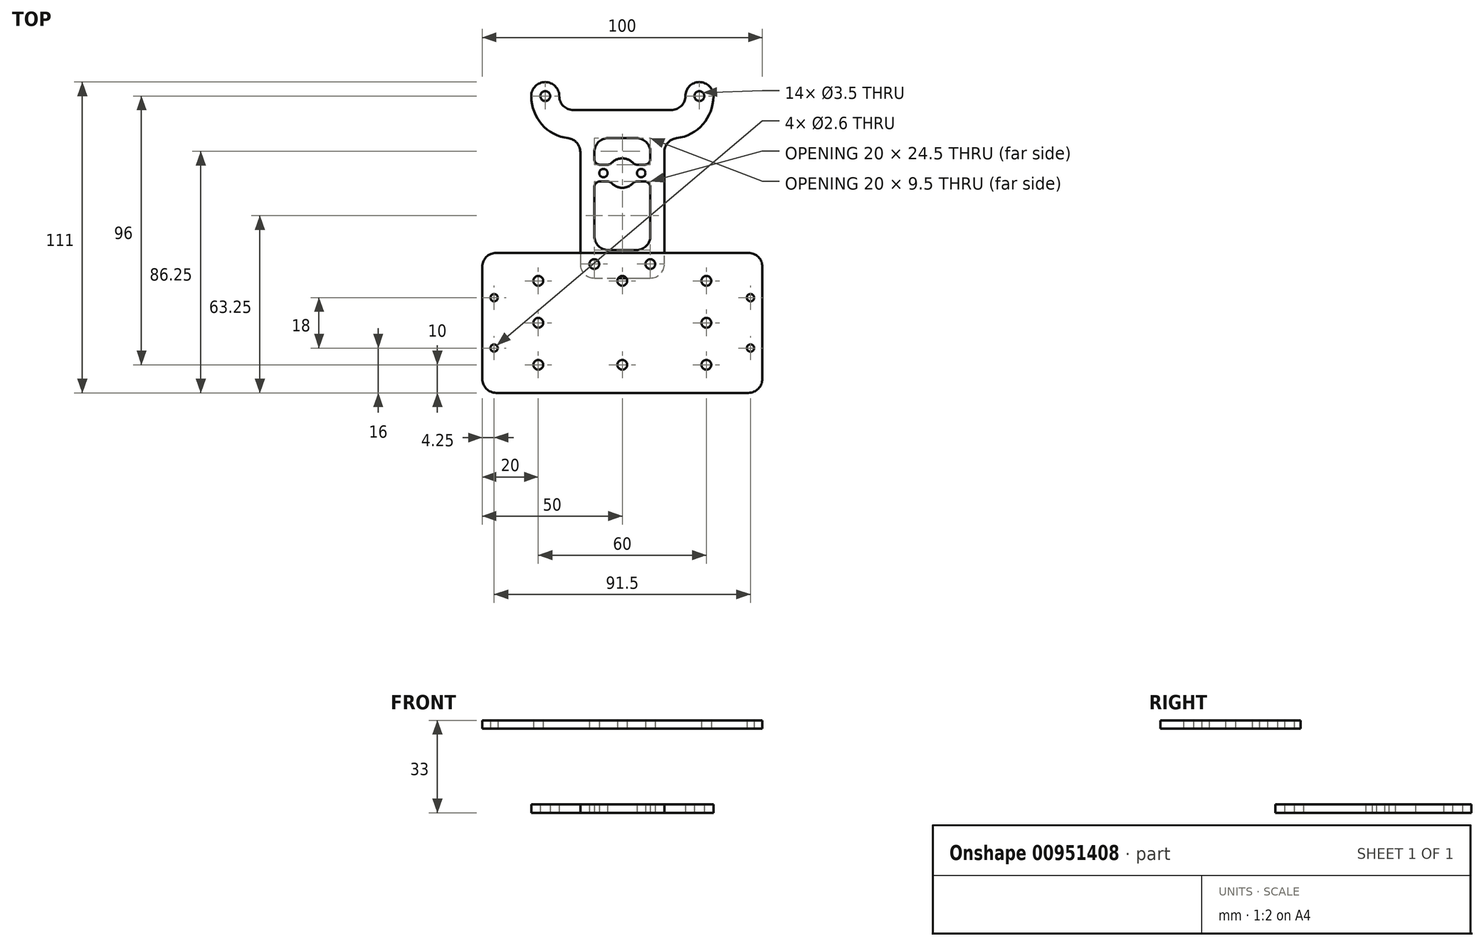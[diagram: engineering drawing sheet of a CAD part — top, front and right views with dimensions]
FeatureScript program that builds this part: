
annotation { "Feature Type Name" : "Feature", "Feature Type Description" : "" }
export const myFeature = defineFeature(function(context is Context, id is Id, definition is map)
    precondition{}
    {
        {
            var Q0;
            Q0=qCreatedBy(makeId("Top.planeOp"),FACE);
            cPlane(context, id + "F0", {"entities" : qUnion([Q0]), "cplaneType" : CPlaneType.OFFSET, "offset" : 30 * mm, "width" : 150 * mm, "height" : 150 * mm});
        }
        {
            var Q0;
            Q0=qCreatedBy(id+"F0.planeOp",FACE);
            var sketch = newSketch(context, id + "F1", { "sketchPlane" : qUnion([Q0])});
            skLineSegment(sketch, "E0.bottom", {"start": v(-25, 30) * mm, "end": v(25, 30) * mm, "construction": true});
            skLineSegment(sketch, "E0.top", {"start": v(-25, -30) * mm, "end": v(25, -30) * mm, "construction": true});
            skLineSegment(sketch, "E0.left", {"start": v(-25, 30) * mm, "end": v(-25, -30) * mm, "construction": true});
            skLineSegment(sketch, "E0.right", {"start": v(25, 30) * mm, "end": v(25, -30) * mm, "construction": true});
            skPoint(sketch, "E0.middle", {"position": v(0, 0) * mm});
            skLineSegment(sketch, "E1.bottom", {"start": v(-60, 42.5) * mm, "end": v(-26, 42.5) * mm, "construction": true});
            skLineSegment(sketch, "E1.top", {"start": v(-60, -42.5) * mm, "end": v(-26, -42.5) * mm, "construction": true});
            skLineSegment(sketch, "E1.left", {"start": v(-60, 42.5) * mm, "end": v(-60, -42.5) * mm, "construction": true});
            skLineSegment(sketch, "E1.right", {"start": v(-26, 42.5) * mm, "end": v(-26, -42.5) * mm, "construction": true});
            skLineSegment(sketch, "E2.bottom", {"start": v(26, 42.5) * mm, "end": v(60, 42.5) * mm, "construction": true});
            skLineSegment(sketch, "E2.top", {"start": v(26, -42.5) * mm, "end": v(60, -42.5) * mm, "construction": true});
            skLineSegment(sketch, "E2.left", {"start": v(26, 42.5) * mm, "end": v(26, -42.5) * mm, "construction": true});
            skLineSegment(sketch, "E2.right", {"start": v(60, 42.5) * mm, "end": v(60, -42.5) * mm, "construction": true});
            skLineSegment(sketch, "E3", {"start": v(0, 0) * mm, "end": v(-26, 0) * mm, "construction": true});
            skLineSegment(sketch, "E4", {"start": v(0, 0) * mm, "end": v(26, 0) * mm, "construction": true});
            skLineSegment(sketch, "E5.bottom", {"start": v(-50, 25) * mm, "end": v(50, 25) * mm});
            skLineSegment(sketch, "E5.top", {"start": v(-50, -25) * mm, "end": v(50, -25) * mm});
            skLineSegment(sketch, "E5.left", {"start": v(-50, 25) * mm, "end": v(-50, 0) * mm});
            skLineSegment(sketch, "E5.right", {"start": v(50, 25) * mm, "end": v(50, 0) * mm});
            skLineSegment(sketch, "E6", {"start": v(-50, 0) * mm, "end": v(-50, -25) * mm});
            skLineSegment(sketch, "E7", {"start": v(50, 0) * mm, "end": v(50, -25) * mm});
            skCircle(sketch, "E8", {"center": v(-45.75, 9) * mm, "radius": 1.3 * mm});
            skCircle(sketch, "E9", {"center": v(-45.75, -9) * mm, "radius": 1.3 * mm});
            skCircle(sketch, "E10", {"center": v(45.75, -9) * mm, "radius": 1.3 * mm});
            skCircle(sketch, "E11", {"center": v(45.75, 9) * mm, "radius": 1.3 * mm});
            skCircle(sketch, "E12", {"center": v(-30, 0) * mm, "radius": 1.75 * mm});
            skCircle(sketch, "E13", {"center": v(30, 0) * mm, "radius": 1.75 * mm});
            skCircle(sketch, "E14", {"center": v(-30, 15) * mm, "radius": 1.75 * mm});
            skCircle(sketch, "E15", {"center": v(30, 15) * mm, "radius": 1.75 * mm});
            skCircle(sketch, "E16", {"center": v(30, -15) * mm, "radius": 1.75 * mm});
            skCircle(sketch, "E17", {"center": v(-30, -15) * mm, "radius": 1.75 * mm});
            skCircle(sketch, "E18", {"center": v(0, 15) * mm, "radius": 1.75 * mm});
            skCircle(sketch, "E19", {"center": v(0, -15) * mm, "radius": 1.75 * mm});
            skCircle(sketch, "E20", {"center": v(-10, 21) * mm, "radius": 1.75 * mm});
            skCircle(sketch, "E21", {"center": v(10, 21) * mm, "radius": 1.75 * mm});
            skSolve(sketch);
        }
        {
            var Q0;
            Q0=makeQuery(id+"F1.imprint","IMPRINT",FACE,{"disambiguationData":[TD([[makeQuery(id+"F1.imprint","IMPRINT",EDGE,{"derivedFrom":sQuery(id+"F1.wireOp",EDGE,"E5.bottom")}),-1.0]])]});
            extrude(context, id + "F2", {"entities" : qUnion([Q0]), "depth" : 3 * mm, "offsetDistance" : 25 * mm});
        }
        {
            var Q0;
            Q0=qCreatedBy(makeId("Top.planeOp"),FACE);
            var sketch = newSketch(context, id + "F3", { "sketchPlane" : qUnion([Q0])});
            skCircle(sketch, "E22.0", {"center": v(-10, 21) * mm, "radius": 1.75 * mm});
            skCircle(sketch, "E22.1", {"center": v(10, 21) * mm, "radius": 1.75 * mm});
            skLineSegment(sketch, "E23", {"start": v(-15, 16) * mm, "end": v(15, 16) * mm});
            skLineSegment(sketch, "E24", {"start": v(15, 16) * mm, "end": v(15, 66) * mm});
            skLineSegment(sketch, "E25", {"start": v(15, 66) * mm, "end": v(32.5, 66) * mm});
            skLineSegment(sketch, "E26", {"start": v(32.5, 66) * mm, "end": v(32.5, 86) * mm});
            skLineSegment(sketch, "E27", {"start": v(32.5, 86) * mm, "end": v(22.5, 86) * mm});
            skLineSegment(sketch, "E28", {"start": v(22.5, 86) * mm, "end": v(22.5, 76) * mm});
            skLineSegment(sketch, "E29", {"start": v(22.5, 76) * mm, "end": v(-22.5, 76) * mm});
            skLineSegment(sketch, "E30", {"start": v(-22.5, 76) * mm, "end": v(-22.5, 86) * mm});
            skLineSegment(sketch, "E31", {"start": v(-22.5, 86) * mm, "end": v(-32.5, 86) * mm});
            skLineSegment(sketch, "E32", {"start": v(-32.5, 86) * mm, "end": v(-32.5, 66) * mm});
            skLineSegment(sketch, "E33", {"start": v(-32.5, 66) * mm, "end": v(-15, 66) * mm});
            skLineSegment(sketch, "E34", {"start": v(-15, 66) * mm, "end": v(-15, 16) * mm});
            skCircle(sketch, "E35", {"center": v(-27.5, 81) * mm, "radius": 1.75 * mm});
            skPoint(sketch, "E35.centerSnap0", {"position": v(-27.5, 86) * mm});
            skPoint(sketch, "E35.centerSnap1", {"position": v(-22.5, 81) * mm});
            skCircle(sketch, "E36", {"center": v(27.5, 81) * mm, "radius": 1.75 * mm});
            skPoint(sketch, "E36.centerSnap0", {"position": v(27.5, 86) * mm});
            skPoint(sketch, "E36.centerSnap1", {"position": v(22.5, 81) * mm});
            skLineSegment(sketch, "E37.bottom", {"start": v(-10, 66) * mm, "end": v(10, 66) * mm});
            skLineSegment(sketch, "E37.top", {"start": v(-10, 26) * mm, "end": v(10, 26) * mm});
            skLineSegment(sketch, "E37.left", {"start": v(-10, 66) * mm, "end": v(-10, 26) * mm});
            skLineSegment(sketch, "E37.right", {"start": v(10, 66) * mm, "end": v(10, 26) * mm});
            skCircle(sketch, "E38", {"center": v(-6.75, 53.5) * mm, "radius": 1.5 * mm});
            skCircle(sketch, "E39", {"center": v(6.75, 53.5) * mm, "radius": 1.5 * mm});
            skLineSegment(sketch, "E40", {"start": v(-6.75, 53.5) * mm, "end": v(-10, 53.5) * mm, "construction": true});
            skLineSegment(sketch, "E41", {"start": v(6.75, 53.5) * mm, "end": v(10, 53.5) * mm, "construction": true});
            skLineSegment(sketch, "E42", {"start": v(-10, 56.5) * mm, "end": v(-4.3, 56.5) * mm});
            skLineSegment(sketch, "E43", {"start": v(10, 50.5) * mm, "end": v(4.3, 50.5) * mm});
            skArc(sketch, "E44", {"start": v(-4.3, 50.5) * mm, "mid": v(0, 48.25) * mm, "end": v(4.3, 50.5) * mm});
            skPoint(sketch, "E44.centerSnap0", {"position": v(0, 66) * mm});
            skArc(sketch, "E45.trimOffspring", {"start": v(4.3, 56.5) * mm, "mid": v(0, 58.75) * mm, "end": v(-4.3, 56.5) * mm});
            skLineSegment(sketch, "E46.trimOffspring", {"start": v(4.3, 56.5) * mm, "end": v(10, 56.5) * mm});
            skLineSegment(sketch, "E47.trimOffspring", {"start": v(-4.3, 50.5) * mm, "end": v(-10, 50.5) * mm});
            skSolve(sketch);
        }
        {
            var Q0;
            Q0=makeQuery(id+"F3.imprint","IMPRINT",FACE,{"disambiguationData":[TD([[makeQuery(id+"F3.imprint","IMPRINT",EDGE,{"derivedFrom":sQuery(id+"F3.wireOp",EDGE,"E22.0")}),-1.0]])]});
            var Q1;
            {var subQ0=sQuery(id+"F3.wireOp",EDGE,"1neENVXK-yCNZ-4XRZ-Vguu-GqOuGw2G458n");Q1=makeQuery(id+"F3.imprint","IMPRINT",FACE,{"disambiguationData":[TD([[makeQuery(id+"F3.imprint","IMPRINT",EDGE,{"derivedFrom":subQ0}),-1.0]])]});}
            var Q2;
            {var subQ5=sQuery(id+"F3.wireOp",EDGE,"E38");Q2=makeQuery(id+"F3.imprint","IMPRINT",FACE,{"disambiguationData":[TD([[makeQuery(id+"F3.imprint","IMPRINT",EDGE,{"derivedFrom":subQ5}),-1.0]])]});}
            var Q3;
            {var subQ0=sQuery(id+"F3.wireOp",EDGE,"6WteCXc5-cXgC-OXwJ-sMJl-BuiwVkrk2LJA");Q3=makeQuery(id+"F3.imprint","IMPRINT",FACE,{"disambiguationData":[TD([[makeQuery(id+"F3.imprint","IMPRINT",EDGE,{"derivedFrom":subQ0}),1.0]])]});}
            extrude(context, id + "F4", {"entities" : qUnion([Q0, Q1, Q2, Q3]), "depth" : 3 * mm, "offsetDistance" : 25 * mm});
        }
        {
            var Q0;
            Q0=makeQuery(id+"F4.opExtrude","SWEPT_EDGE",EDGE,{"disambiguationData":[OSD([sQuery(id+"F3.wireOp",EDGE,"E33"),sQuery(id+"F3.wireOp",EDGE,"E34")])]});
            var Q1;
            Q1=makeQuery(id+"F4.opExtrude","SWEPT_EDGE",EDGE,{"disambiguationData":[OSD([sQuery(id+"F3.wireOp",EDGE,"E29"),sQuery(id+"F3.wireOp",EDGE,"E30")])]});
            var Q2;
            Q2=makeQuery(id+"F4.opExtrude","SWEPT_EDGE",EDGE,{"disambiguationData":[OSD([sQuery(id+"F3.wireOp",EDGE,"E30"),sQuery(id+"F3.wireOp",EDGE,"E31")])]});
            var Q3;
            Q3=makeQuery(id+"F4.opExtrude","SWEPT_EDGE",EDGE,{"disambiguationData":[OSD([sQuery(id+"F3.wireOp",EDGE,"E31"),sQuery(id+"F3.wireOp",EDGE,"E32")])]});
            var Q4;
            Q4=makeQuery(id+"F4.opExtrude","SWEPT_EDGE",EDGE,{"disambiguationData":[OSD([sQuery(id+"F3.wireOp",EDGE,"E28"),sQuery(id+"F3.wireOp",EDGE,"E29")])]});
            var Q5;
            Q5=makeQuery(id+"F4.opExtrude","SWEPT_EDGE",EDGE,{"disambiguationData":[OSD([sQuery(id+"F3.wireOp",EDGE,"E27"),sQuery(id+"F3.wireOp",EDGE,"E28")])]});
            var Q6;
            Q6=makeQuery(id+"F4.opExtrude","SWEPT_EDGE",EDGE,{"disambiguationData":[OSD([sQuery(id+"F3.wireOp",EDGE,"E26"),sQuery(id+"F3.wireOp",EDGE,"E27")])]});
            var Q7;
            Q7=makeQuery(id+"F4.opExtrude","SWEPT_EDGE",EDGE,{"disambiguationData":[OSD([sQuery(id+"F3.wireOp",EDGE,"E24"),sQuery(id+"F3.wireOp",EDGE,"E25")])]});
            var Q8;
            Q8=makeQuery(id+"F4.opExtrude","SWEPT_EDGE",EDGE,{"disambiguationData":[OSD([sQuery(id+"F3.wireOp",EDGE,"E23"),sQuery(id+"F3.wireOp",EDGE,"E24")])]});
            var Q9;
            Q9=makeQuery(id+"F4.opExtrude","SWEPT_EDGE",EDGE,{"disambiguationData":[OSD([sQuery(id+"F3.wireOp",EDGE,"E23"),sQuery(id+"F3.wireOp",EDGE,"E34")])]});
            var Q10;
            Q10=makeQuery(id+"F4.opExtrude","SWEPT_EDGE",EDGE,{"disambiguationData":[OSD([sQuery(id+"F3.wireOp",EDGE,"E37.bottom"),sQuery(id+"F3.wireOp",EDGE,"E37.left")])]});
            var Q11;
            Q11=makeQuery(id+"F4.opExtrude","SWEPT_EDGE",EDGE,{"disambiguationData":[OSD([sQuery(id+"F3.wireOp",EDGE,"E37.bottom"),sQuery(id+"F3.wireOp",EDGE,"E37.right")])]});
            var Q12;
            Q12=makeQuery(id+"F4.opExtrude","SWEPT_EDGE",EDGE,{"disambiguationData":[OSD([sQuery(id+"F3.wireOp",EDGE,"E37.top"),sQuery(id+"F3.wireOp",EDGE,"E37.right")])]});
            var Q13;
            Q13=makeQuery(id+"F4.opExtrude","SWEPT_EDGE",EDGE,{"disambiguationData":[OSD([sQuery(id+"F3.wireOp",EDGE,"E37.top"),sQuery(id+"F3.wireOp",EDGE,"E37.left")])]});
            fillet(context, id + "F5", {"entities" : qUnion([Q0, Q1, Q2, Q3, Q4, Q5, Q6, Q7, Q8, Q9, Q10, Q11, Q12, Q13]), "radius" : 5 * mm, "tangentPropagation" : true, "allowEdgeOverflow" : false});
        }
        {
            var Q0;
            Q0=makeQuery(id+"F4.opExtrude","SWEPT_EDGE",EDGE,{"disambiguationData":[OSD([sQuery(id+"F3.wireOp",EDGE,"E25"),sQuery(id+"F3.wireOp",EDGE,"E26")])]});
            var Q1;
            Q1=makeQuery(id+"F4.opExtrude","SWEPT_EDGE",EDGE,{"disambiguationData":[OSD([sQuery(id+"F3.wireOp",EDGE,"E32"),sQuery(id+"F3.wireOp",EDGE,"E33")])]});
            fillet(context, id + "F6", {"entities" : qUnion([Q0, Q1]), "radius" : 15 * mm, "tangentPropagation" : true, "allowEdgeOverflow" : false});
        }
        {
            var Q0;
            Q0=makeQuery(id+"F2.opExtrude","SWEPT_EDGE",EDGE,{"disambiguationData":[OSD([sQuery(id+"F1.wireOp",EDGE,"E5.bottom"),sQuery(id+"F1.wireOp",EDGE,"E5.left")])]});
            var Q1;
            Q1=makeQuery(id+"F2.opExtrude","SWEPT_EDGE",EDGE,{"disambiguationData":[OSD([sQuery(id+"F1.wireOp",EDGE,"E5.top"),sQuery(id+"F1.wireOp",EDGE,"E6")])]});
            var Q2;
            Q2=makeQuery(id+"F2.opExtrude","SWEPT_EDGE",EDGE,{"disambiguationData":[OSD([sQuery(id+"F1.wireOp",EDGE,"E5.top"),sQuery(id+"F1.wireOp",EDGE,"E7")])]});
            var Q3;
            Q3=makeQuery(id+"F2.opExtrude","SWEPT_EDGE",EDGE,{"disambiguationData":[OSD([sQuery(id+"F1.wireOp",EDGE,"E5.bottom"),sQuery(id+"F1.wireOp",EDGE,"E5.right")])]});
            fillet(context, id + "F7", {"entities" : qUnion([Q0, Q1, Q2, Q3]), "radius" : 5 * mm, "tangentPropagation" : true, "allowEdgeOverflow" : false});
        }
        {
            var Q0;
            Q0=makeQuery(id+"F4.opExtrude","SWEPT_EDGE",EDGE,{"disambiguationData":[OSD([sQuery(id+"F3.wireOp",EDGE,"E37.left"),sQuery(id+"F3.wireOp",EDGE,"E42")])]});
            var Q1;
            Q1=makeQuery(id+"F4.opExtrude","SWEPT_EDGE",EDGE,{"disambiguationData":[OSD([sQuery(id+"F3.wireOp",EDGE,"E37.left"),sQuery(id+"F3.wireOp",EDGE,"E47.trimOffspring")])]});
            var Q2;
            Q2=makeQuery(id+"F4.opExtrude","SWEPT_EDGE",EDGE,{"disambiguationData":[OSD([sQuery(id+"F3.wireOp",EDGE,"E37.right"),sQuery(id+"F3.wireOp",EDGE,"E43")])]});
            var Q3;
            Q3=makeQuery(id+"F4.opExtrude","SWEPT_EDGE",EDGE,{"disambiguationData":[OSD([sQuery(id+"F3.wireOp",EDGE,"E37.right"),sQuery(id+"F3.wireOp",EDGE,"E46.trimOffspring")])]});
            var Q4;
            Q4=makeQuery(id+"F4.opExtrude","SWEPT_EDGE",EDGE,{"disambiguationData":[OSD([sQuery(id+"F3.wireOp",EDGE,"E45.trimOffspring"),sQuery(id+"F3.wireOp",EDGE,"E46.trimOffspring")])]});
            var Q5;
            Q5=makeQuery(id+"F4.opExtrude","SWEPT_EDGE",EDGE,{"disambiguationData":[OSD([sQuery(id+"F3.wireOp",EDGE,"E42"),sQuery(id+"F3.wireOp",EDGE,"E45.trimOffspring")])]});
            var Q6;
            Q6=makeQuery(id+"F4.opExtrude","SWEPT_EDGE",EDGE,{"disambiguationData":[OSD([sQuery(id+"F3.wireOp",EDGE,"E44"),sQuery(id+"F3.wireOp",EDGE,"E47.trimOffspring")])]});
            var Q7;
            Q7=makeQuery(id+"F4.opExtrude","SWEPT_EDGE",EDGE,{"disambiguationData":[OSD([sQuery(id+"F3.wireOp",EDGE,"E43"),sQuery(id+"F3.wireOp",EDGE,"E44")])]});
            fillet(context, id + "F8", {"entities" : qUnion([Q0, Q1, Q2, Q3, Q4, Q5, Q6, Q7]), "radius" : 2 * mm, "tangentPropagation" : true, "allowEdgeOverflow" : false});
        }
    });
